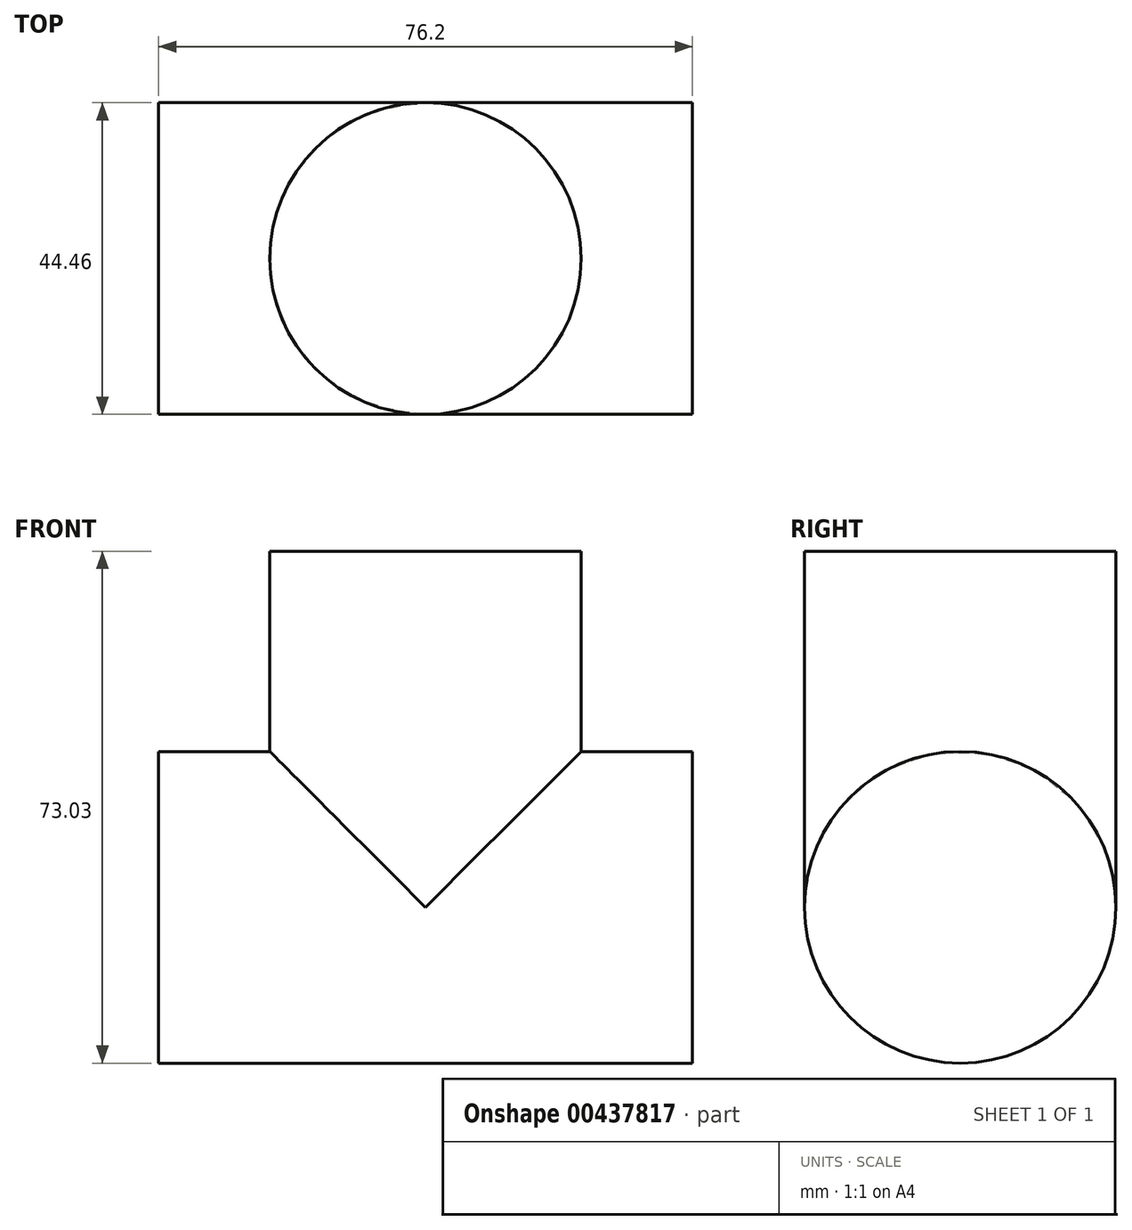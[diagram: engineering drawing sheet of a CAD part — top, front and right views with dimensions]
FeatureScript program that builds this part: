
annotation { "Feature Type Name" : "Feature", "Feature Type Description" : "" }
export const myFeature = defineFeature(function(context is Context, id is Id, definition is map)
    precondition{}
    {
        {
            var Q0;
            Q0=qCreatedBy(makeId("Top.planeOp"),FACE);
            var sketch = newSketch(context, id + "F0", { "sketchPlane" : qUnion([Q0])});
            skCircle(sketch, "E0", {"center": v(0, 0) * mm, "radius": 22.22 * mm});
            skSolve(sketch);
        }
        {
            var Q0;
            Q0=qCreatedBy(makeId("Right.planeOp"),FACE);
            var sketch = newSketch(context, id + "F1", { "sketchPlane" : qUnion([Q0])});
            skCircle(sketch, "E1", {"center": v(0, 0) * mm, "radius": 22.23 * mm});
            skSolve(sketch);
        }
        {
            var Q0;
            Q0=makeQuery(id+"F1.imprint","IMPRINT",FACE,{"disambiguationData":[TD([[makeQuery(id+"F1.imprint","IMPRINT",EDGE,{"derivedFrom":sQuery(id+"F1.wireOp",EDGE,"E1")}),1.0]])]});
            extrude(context, id + "F2", {"entities" : qUnion([Q0]), "endBound" : BoundingType.SYMMETRIC, "depth" : 76.2 * mm});
        }
        {
            var Q0;
            Q0=makeQuery(id+"F0.imprint","IMPRINT",FACE,{"disambiguationData":[TD([[makeQuery(id+"F0.imprint","IMPRINT",EDGE,{"derivedFrom":sQuery(id+"F0.wireOp",EDGE,"E0")}),1.0]])]});
            extrude(context, id + "F3", {"entities" : qUnion([Q0]), "operationType" : NewBodyOperationType.ADD, "depth" : 50.8 * mm});
        }
    });
